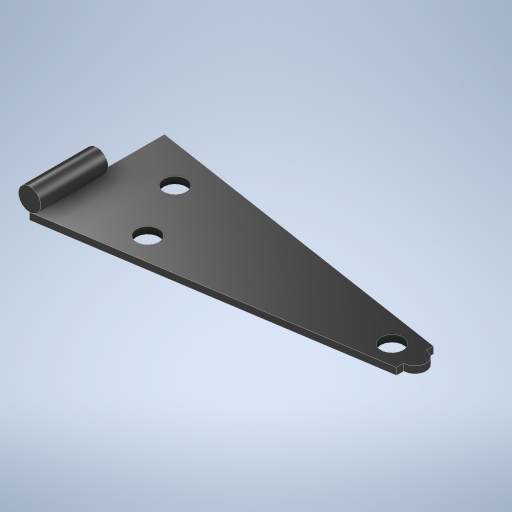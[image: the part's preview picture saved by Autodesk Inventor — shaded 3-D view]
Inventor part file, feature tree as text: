
AUTODESK INVENTOR PART (.ipt)
format: ipt  version: 2024 (Build 280153000, 153)  size: 265,216 bytes
history: native  units: in
note: dims shown in document units (in); Inventor stores cm internally (conversion verified against a paired STEP export)
features: extrude x2, sketch x2
ambient origin geometry x8: Origin, YZ Plane, XZ Plane, XY Plane, X Axis, Y Axis, Z Axis, Center Point
bodies: Solid1 (feature_tree)
feature tree (4):
  extrude  "Extrusion1"  Depth=0.59in
  extrude  "Extrusion2"  Depth=0.06in
  sketch  "Sketch1"  dims[d0=2.88in d1=0.59in]
  sketch  "Sketch2"  dims[d2=1.18in d3=0.1969in d4=0.0984in d5=0.063in d6=0.1969in d7=0.1969in d8=0.1969in d9=0.25in d10=0.25in d11=0.06in d12=0.0in d13=0.0984in d14=0.06in d15=0.0in]
